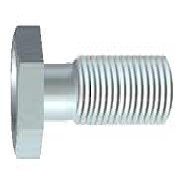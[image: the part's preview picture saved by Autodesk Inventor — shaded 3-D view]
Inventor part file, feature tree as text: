
AUTODESK INVENTOR PART (.ipt)
format: ipt  version: 2014 (Build 180170000, 170)  size: 177,664 bytes
history: native  units: mm (DEFAULTED — no unit token found)
features: sketch x4, extrude x2, chamfer x1, plane x1
ambient origin geometry x7: Origin, YZ Plane, XZ Plane, X Axis, Y Axis, Z Axis, Center Point
bodies: Solid1 (feature_tree), Body (feature_tree)
feature tree (8):
  extrude  "Head"  TaperAngle=90.0deg  [1 undecoded]
  extrude  "Indent"  TaperAngle=0.0deg  [1 undecoded]
  chamfer  "Chamfer1"  Distance=0.39751mm
  plane  "Work Plane1"
  sketch  "Sketch1"  dims[d1=4.1656mm d12=90.0deg]
  sketch  "Sketch2"  dims[d2=2.794mm d3=0.0mm]
  sketch  "Sketch4"  dims[d21=90.0deg d5=0.39751mm d6=0.39761mm d7=0.0mm d8=7.9248mm d9=26.9875mm d10=0.0mm d13=31.75mm d17=7.9248mm d18=6.33984mm d19=0.2804mm d20=0.0mm d77=45.0deg d80=0.0mm d81=0.0mm]
  sketch  "Sketch3"  dims[d4=30.0deg]
note: 2 required parameter values undecoded (feature->parameter linkage not recoverable at this tier; creation-order binding heuristic only, values carry confidence <= 0.55)
